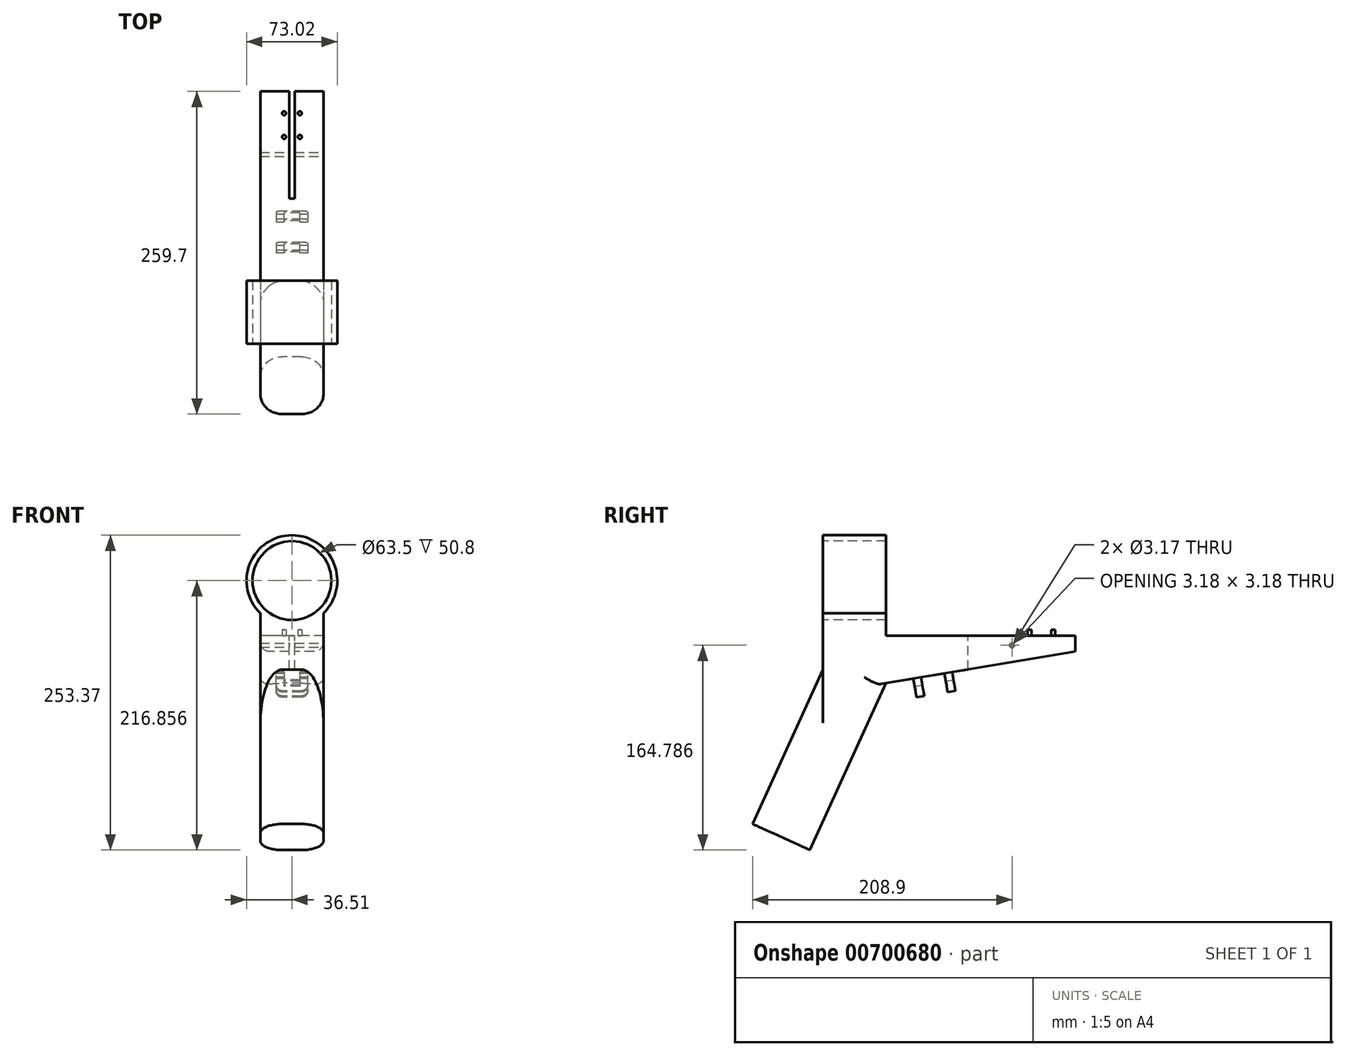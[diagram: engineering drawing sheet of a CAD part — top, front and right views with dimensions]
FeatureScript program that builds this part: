
annotation { "Feature Type Name" : "Feature", "Feature Type Description" : "" }
export const myFeature = defineFeature(function(context is Context, id is Id, definition is map)
    precondition{}
    {
        {
            var Q0;
            Q0=qCreatedBy(makeId("Right.planeOp"),FACE);
            var sketch = newSketch(context, id + "F0", { "sketchPlane" : qUnion([Q0])});
            skLineSegment(sketch, "E0", {"start": v(0, 0) * mm, "end": v(0, 39.8) * mm});
            skLineSegment(sketch, "E1", {"start": v(0, 39.8) * mm, "end": v(50.8, 39.8) * mm});
            skLineSegment(sketch, "E2", {"start": v(50.8, 39.8) * mm, "end": v(50.8, 27.1) * mm});
            skLineSegment(sketch, "E3", {"start": v(50.8, 27.1) * mm, "end": v(203.2, 27.1) * mm});
            skLineSegment(sketch, "E4", {"start": v(203.2, 27.1) * mm, "end": v(203.2, 14.4) * mm});
            skLineSegment(sketch, "E5", {"start": v(203.2, 14.4) * mm, "end": v(50.8, -11) * mm});
            skLineSegment(sketch, "E6", {"start": v(50.8, -11) * mm, "end": v(-10.25, -145.31) * mm});
            skLineSegment(sketch, "E7", {"start": v(-10.25, -145.31) * mm, "end": v(-56.5, -124.3) * mm});
            skLineSegment(sketch, "E8", {"start": v(-56.5, -124.3) * mm, "end": v(0, 0) * mm});
            skSolve(sketch);
        }
        {
            var Q0;
            Q0 = qSketchRegion(id + "F0", true);
            extrude(context, id + "F1", {"entities" : qUnion([Q0]), "depth" : 50.8 * mm, "offsetDistance" : 25.4 * mm});
        }
        {
            var Q0;
            Q0=makeQuery(id+"F1.opExtrude","SWEPT_FACE",FACE,{"disambiguationData":[OSD([sQuery(id+"F0.wireOp",EDGE,"E0")])]});
            var sketch = newSketch(context, id + "F2", { "sketchPlane" : qUnion([Q0])});
            skCircle(sketch, "E9", {"center": v(25.4, 71.55) * mm, "radius": 31.75 * mm});
            skPoint(sketch, "E10", {"position": v(25.4, 39.8) * mm});
            skLineSegment(sketch, "E11", {"start": v(0, 39.8) * mm, "end": v(0, 45.32) * mm});
            skLineSegment(sketch, "E12", {"start": v(50.8, 39.8) * mm, "end": v(50.8, 45.32) * mm});
            skPoint(sketch, "E13", {"position": v(7.37, 39.8) * mm});
            skPoint(sketch, "E14", {"position": v(43.43, 39.8) * mm});
            skArc(sketch, "E15.trimOffspring", {"start": v(50.8, 45.32) * mm, "mid": v(25.4, 108.06) * mm, "end": v(0, 45.32) * mm});
            skLineSegment(sketch, "E16", {"start": v(0, 39.8) * mm, "end": v(7.37, 39.8) * mm});
            skLineSegment(sketch, "E17", {"start": v(50.8, 39.8) * mm, "end": v(43.43, 39.8) * mm});
            skArc(sketch, "E18", {"start": v(7.37, 39.8) * mm, "mid": v(25.4, 35.03) * mm, "end": v(43.43, 39.8) * mm});
            skSolve(sketch);
        }
        {
            var Q0;
            Q0 = qSketchRegion(id + "F2", true);
            extrude(context, id + "F3", {"entities" : qUnion([Q0]), "operationType" : NewBodyOperationType.ADD, "oppositeDirection" : true, "depth" : 50.8 * mm, "offsetDistance" : 25.4 * mm});
        }
        {
            var Q0;
            Q0=makeQuery(id+"F1.opExtrude","CAP_EDGE",EDGE,{"disambiguationData":[OSD([sQuery(id+"F0.wireOp",EDGE,"E8")])],"isStart":false});
            var Q1;
            Q1=makeQuery(id+"F1.opExtrude","CAP_EDGE",EDGE,{"disambiguationData":[OSD([sQuery(id+"F0.wireOp",EDGE,"E8")])],"isStart":true});
            var Q2;
            Q2=makeQuery(id+"F1.opExtrude","CAP_EDGE",EDGE,{"disambiguationData":[OSD([sQuery(id+"F0.wireOp",EDGE,"E6")])],"isStart":false});
            var Q3;
            Q3=makeQuery(id+"F1.opExtrude","CAP_EDGE",EDGE,{"disambiguationData":[OSD([sQuery(id+"F0.wireOp",EDGE,"E6")])],"isStart":true});
            fillet(context, id + "F4", {"entities" : qUnion([Q0, Q1, Q2, Q3]), "radius" : 17.78 * mm, "tangentPropagation" : true, "allowEdgeOverflow" : false});
        }
        {
            var Q0;
            Q0=makeQuery(id+"F1.opExtrude","CAP_EDGE",EDGE,{"disambiguationData":[OSD([sQuery(id+"F0.wireOp",EDGE,"E5")])],"isStart":false});
            var Q1;
            Q1=makeQuery(id+"F1.opExtrude","CAP_EDGE",EDGE,{"disambiguationData":[OSD([sQuery(id+"F0.wireOp",EDGE,"E5")])],"isStart":true});
            fillet(context, id + "F5", {"entities" : qUnion([Q0, Q1]), "radius" : 7.62 * mm, "tangentPropagation" : true, "allowEdgeOverflow" : false});
        }
        {
            var Q0;
            Q0=makeQuery(id+"F1.opExtrude","SWEPT_FACE",FACE,{"disambiguationData":[OSD([sQuery(id+"F0.wireOp",EDGE,"E3")])]});
            var sketch = newSketch(context, id + "F6", { "sketchPlane" : qUnion([Q0])});
            skPoint(sketch, "E19", {"position": v(25.4, 203.2) * mm});
            skPoint(sketch, "E20", {"position": v(25.4, 185.64) * mm});
            skCircle(sketch, "E21", {"center": v(19.05, 185.64) * mm, "radius": 1.59 * mm});
            skCircle(sketch, "E22", {"center": v(31.75, 185.64) * mm, "radius": 1.59 * mm});
            skCircle(sketch, "E23", {"center": v(31.75, 166.59) * mm, "radius": 1.59 * mm});
            skCircle(sketch, "E24", {"center": v(19.05, 166.59) * mm, "radius": 1.59 * mm});
            skSolve(sketch);
        }
        {
            var Q0;
            Q0 = qSketchRegion(id + "F6", true);
            extrude(context, id + "F7", {"entities" : qUnion([Q0]), "operationType" : NewBodyOperationType.ADD, "depth" : 4.76 * mm, "offsetDistance" : 25.4 * mm});
        }
        {
            var Q0;
            Q0=makeQuery(id+"F1.opExtrude","SWEPT_FACE",FACE,{"disambiguationData":[OSD([sQuery(id+"F0.wireOp",EDGE,"E3")])]});
            var sketch = newSketch(context, id + "F8", { "sketchPlane" : qUnion([Q0])});
            skLineSegment(sketch, "E25.bottom", {"start": v(23.11, 203.2) * mm, "end": v(27.69, 203.2) * mm});
            skLineSegment(sketch, "E25.top", {"start": v(23.11, 116.84) * mm, "end": v(27.69, 116.84) * mm});
            skLineSegment(sketch, "E25.left", {"start": v(23.11, 203.2) * mm, "end": v(23.11, 116.84) * mm});
            skLineSegment(sketch, "E25.right", {"start": v(27.69, 203.2) * mm, "end": v(27.69, 116.84) * mm});
            skPoint(sketch, "E26", {"position": v(25.4, 203.2) * mm});
            skSolve(sketch);
        }
        {
            var Q0;
            Q0 = qSketchRegion(id + "F8", true);
            extrude(context, id + "F9", {"entities" : qUnion([Q0]), "operationType" : NewBodyOperationType.REMOVE, "oppositeDirection" : true, "depth" : 127 * mm, "offsetDistance" : 25.4 * mm});
        }
        {
            var Q0;
            Q0=makeQuery(id+"F3.boolean.opBoolean","MERGE",FACE,{"derivedFrom":[makeQuery(id+"F1.opExtrude","CAP_FACE",FACE,{"disambiguationData":[OSD([sQuery(id+"F0.wireOp",EDGE,"E0"),sQuery(id+"F0.wireOp",EDGE,"E1"),sQuery(id+"F0.wireOp",EDGE,"E2"),sQuery(id+"F0.wireOp",EDGE,"E3"),sQuery(id+"F0.wireOp",EDGE,"E4"),sQuery(id+"F0.wireOp",EDGE,"E5"),sQuery(id+"F0.wireOp",EDGE,"E6"),sQuery(id+"F0.wireOp",EDGE,"E7"),sQuery(id+"F0.wireOp",EDGE,"E8")])],"isStart":false}),makeQuery(id+"F3.opExtrude","SWEPT_FACE",FACE,{"disambiguationData":[OSD([sQuery(id+"F2.wireOp",EDGE,"E12")])]})]});
            var sketch = newSketch(context, id + "F10", { "sketchPlane" : qUnion([Q0])});
            skPoint(sketch, "E27", {"position": v(152.4, 19.48) * mm});
            skSolve(sketch);
        }
        {
            var Q0;
            Q0=sQuery(id+"F10.wireOp",VERTEX,"E27");
            var Q1;
            Q1=makeQuery(id+"F1.opExtrude","SWEPT_BODY",BODY,{"disambiguationData":[OSD([sQuery(id+"F0.wireOp",EDGE,"E0"),sQuery(id+"F0.wireOp",EDGE,"E1"),sQuery(id+"F0.wireOp",EDGE,"E2"),sQuery(id+"F0.wireOp",EDGE,"E3"),sQuery(id+"F0.wireOp",EDGE,"E4"),sQuery(id+"F0.wireOp",EDGE,"E5"),sQuery(id+"F0.wireOp",EDGE,"E6"),sQuery(id+"F0.wireOp",EDGE,"E7"),sQuery(id+"F0.wireOp",EDGE,"E8")])]});
            hole(context, id + "F11", {"style" : HoleStyle.SIMPLE, "endStyle" : HoleEndStyle.THROUGH, "holeDiameter" : 3.17 * mm, "majorDiameter" : 6.35 * mm, "isTappedThrough" : true, "tappedDepth" : 12.7 * mm, "tapClearance" : 3, "startFromSketch" : true, "locations" : qUnion([Q0]), "scope" : qUnion([Q1])});
        }
        {
            var Q0;
            Q0=makeQuery(id+"F1.opExtrude","SWEPT_FACE",FACE,{"disambiguationData":[OSD([sQuery(id+"F0.wireOp",EDGE,"E5")])]});
            var sketch = newSketch(context, id + "F12", { "sketchPlane" : qUnion([Q0])});
            skLineSegment(sketch, "E28.bottom", {"start": v(38.1, -102.55) * mm, "end": v(12.7, -102.55) * mm});
            skLineSegment(sketch, "E28.top", {"start": v(38.1, -96.2) * mm, "end": v(12.7, -96.2) * mm});
            skLineSegment(sketch, "E28.left", {"start": v(38.1, -102.55) * mm, "end": v(38.1, -96.2) * mm});
            skLineSegment(sketch, "E28.right", {"start": v(12.7, -102.55) * mm, "end": v(12.7, -96.2) * mm});
            skLineSegment(sketch, "E29.bottom", {"start": v(38.1, -77.15) * mm, "end": v(12.7, -77.15) * mm});
            skLineSegment(sketch, "E29.top", {"start": v(38.1, -70.8) * mm, "end": v(12.7, -70.8) * mm});
            skLineSegment(sketch, "E29.left", {"start": v(38.1, -77.15) * mm, "end": v(38.1, -70.8) * mm});
            skLineSegment(sketch, "E29.right", {"start": v(12.7, -77.15) * mm, "end": v(12.7, -70.8) * mm});
            skPoint(sketch, "E30", {"position": v(25.4, -102.55) * mm});
            skPoint(sketch, "E31", {"position": v(25.4, -77.15) * mm});
            skPoint(sketch, "E32", {"position": v(25.4, -115.25) * mm});
            skSolve(sketch);
        }
        {
            var Q0;
            Q0 = qSketchRegion(id + "F12", true);
            extrude(context, id + "F13", {"entities" : qUnion([Q0]), "operationType" : NewBodyOperationType.ADD, "depth" : 15.24 * mm, "offsetDistance" : 25.4 * mm});
        }
        {
            var Q0;
            Q0=makeQuery(id+"F13.opExtrude","CAP_EDGE",EDGE,{"disambiguationData":[OSD([sQuery(id+"F12.wireOp",EDGE,"E28.left")])],"isStart":false});
            var Q1;
            Q1=makeQuery(id+"F13.opExtrude","CAP_EDGE",EDGE,{"disambiguationData":[OSD([sQuery(id+"F12.wireOp",EDGE,"E29.left")])],"isStart":false});
            var Q2;
            Q2=makeQuery(id+"F13.opExtrude","CAP_EDGE",EDGE,{"disambiguationData":[OSD([sQuery(id+"F12.wireOp",EDGE,"E29.right")])],"isStart":false});
            var Q3;
            Q3=makeQuery(id+"F13.opExtrude","CAP_EDGE",EDGE,{"disambiguationData":[OSD([sQuery(id+"F12.wireOp",EDGE,"E28.right")])],"isStart":false});
            fillet(context, id + "F14", {"entities" : qUnion([Q0, Q1, Q2, Q3]), "radius" : 5.08 * mm, "tangentPropagation" : true, "allowEdgeOverflow" : false});
        }
        {
            var Q0;
            Q0=makeQuery(id+"F13.opExtrude","SWEPT_FACE",FACE,{"disambiguationData":[OSD([sQuery(id+"F12.wireOp",EDGE,"E28.bottom")])]});
            var sketch = newSketch(context, id + "F15", { "sketchPlane" : qUnion([Q0])});
            skLineSegment(sketch, "E33.bottom", {"start": v(-31.75, -19.2) * mm, "end": v(-19.05, -19.2) * mm});
            skLineSegment(sketch, "E33.top", {"start": v(-31.75, -25.56) * mm, "end": v(-19.05, -25.56) * mm});
            skLineSegment(sketch, "E33.left", {"start": v(-31.75, -19.2) * mm, "end": v(-31.75, -25.56) * mm});
            skLineSegment(sketch, "E33.right", {"start": v(-19.05, -19.2) * mm, "end": v(-19.05, -25.56) * mm});
            skPoint(sketch, "E34", {"position": v(-25.4, -19.2) * mm});
            skSolve(sketch);
        }
        {
            var Q0;
            Q0 = qSketchRegion(id + "F15", true);
            extrude(context, id + "F16", {"entities" : qUnion([Q0]), "operationType" : NewBodyOperationType.REMOVE, "oppositeDirection" : true, "depth" : 50.8 * mm, "offsetDistance" : 25.4 * mm});
        }
    });
